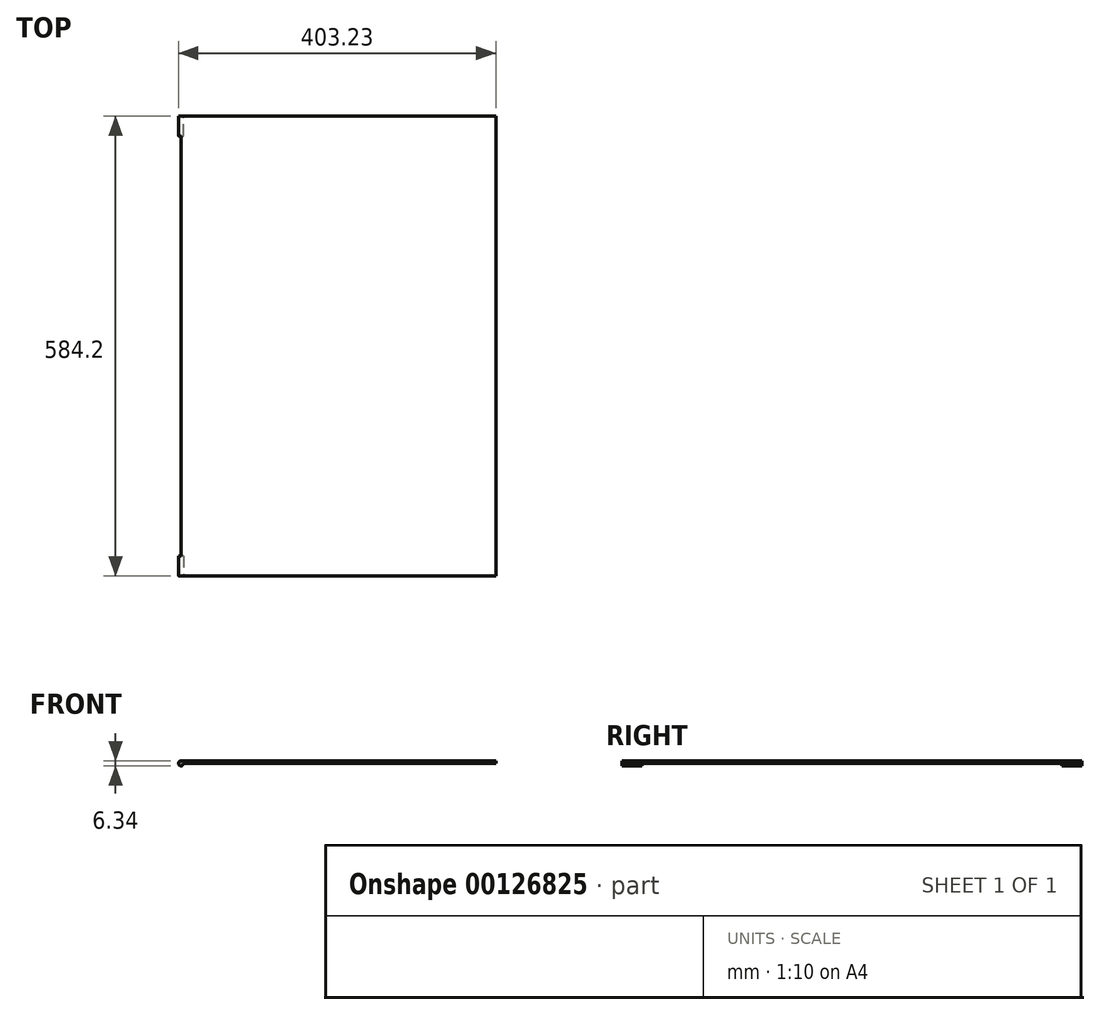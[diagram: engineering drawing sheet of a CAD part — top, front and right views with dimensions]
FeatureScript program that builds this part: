
annotation { "Feature Type Name" : "Feature", "Feature Type Description" : "" }
export const myFeature = defineFeature(function(context is Context, id is Id, definition is map)
    precondition{}
    {
        {
            var Q0;
            Q0=qCreatedBy(makeId("Top.planeOp"),FACE);
            var sketch = newSketch(context, id + "F0", { "sketchPlane" : qUnion([Q0])});
            skLineSegment(sketch, "E0.bottom", {"start": v(200.03, 292.1) * mm, "end": v(-200.03, 292.1) * mm});
            skLineSegment(sketch, "E0.top", {"start": v(200.03, -292.1) * mm, "end": v(-200.03, -292.1) * mm});
            skLineSegment(sketch, "E0.left", {"start": v(200.03, 292.1) * mm, "end": v(200.03, -292.1) * mm});
            skLineSegment(sketch, "E0.right", {"start": v(-200.03, 292.1) * mm, "end": v(-200.03, -292.1) * mm});
            skPoint(sketch, "E0.middle", {"position": v(0, 0) * mm});
            skSolve(sketch);
        }
        {
            var Q0;
            Q0=makeQuery(id+"F0.imprint","IMPRINT",FACE,{"disambiguationData":[TD([[makeQuery(id+"F0.imprint","IMPRINT",EDGE,{"derivedFrom":sQuery(id+"F0.wireOp",EDGE,"E0.bottom")}),1.0]])]});
            extrude(context, id + "F1", {"entities" : qUnion([Q0]), "depth" : 3.17 * mm});
        }
        {
            var Q0;
            Q0=makeQuery(id+"F1.opExtrude","SWEPT_FACE",FACE,{"disambiguationData":[OSD([sQuery(id+"F0.wireOp",EDGE,"E0.top")])]});
            var sketch = newSketch(context, id + "F2", { "sketchPlane" : qUnion([Q0])});
            skCircle(sketch, "E1", {"center": v(-200.03, 0) * mm, "radius": 3.18 * mm});
            skSolve(sketch);
        }
        {
            var Q0;
            {var subQ1=sQuery(id+"F0.wireOp",EDGE,"E0.top");var subQ2=makeQuery(id+"F1.opExtrude","SWEPT_EDGE",EDGE,{"disambiguationData":[OSD([subQ1,sQuery(id+"F0.wireOp",EDGE,"E0.right")])]});Q0=makeQuery(id+"F2.imprint","IMPRINT",FACE,{"disambiguationData":[TD([[makeQuery(id+"F2.imprint","IMPRINT",EDGE,{"derivedFrom":subQ2}),-1.0]])]});}
            extrude(context, id + "F3", {"entities" : qUnion([Q0]), "oppositeDirection" : true, "depth" : 25.4 * mm});
        }
        {
            var Q0;
            Q0=makeQuery(id+"F3.opExtrude","SWEPT_BODY",BODY,{"disambiguationData":[OSD([sQuery(id+"F0.wireOp",EDGE,"E0.top"),sQuery(id+"F0.wireOp",EDGE,"E0.right"),sQuery(id+"F2.wireOp",EDGE,"E1")])]});
            var Q1;
            Q1=qCreatedBy(makeId("Front.planeOp"),FACE);
            mirror(context, id + "F4", {"operationType" : NewBodyOperationType.ADD, "entities" : qUnion([Q0]), "mirrorPlane" : qUnion([Q1])});
        }
    });
